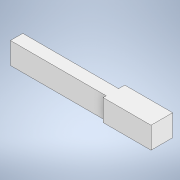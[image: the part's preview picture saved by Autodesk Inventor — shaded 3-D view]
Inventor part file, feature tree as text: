
AUTODESK INVENTOR PART (.ipt)
format: ipt  version: 2021 (Build 250183000, 183)  size: 99,840 bytes
history: native  units: in
note: dims shown in document units (in); Inventor stores cm internally (conversion verified against a paired STEP export)
features: extrude x1, sketch x1
ambient origin geometry x8: Origin, YZ Plane, XZ Plane, XY Plane, X Axis, Y Axis, Z Axis, Center Point
bodies: Solid1 (feature_tree)
feature tree (2):
  extrude  "Extrusion1"  Depth=5.8125in
  sketch  "Sketch1"  dims[d0=0.875in d1=5.8125in d2=3.875in d4=0.625in d5=0.75in d6=0.875in d7=0.0in]
